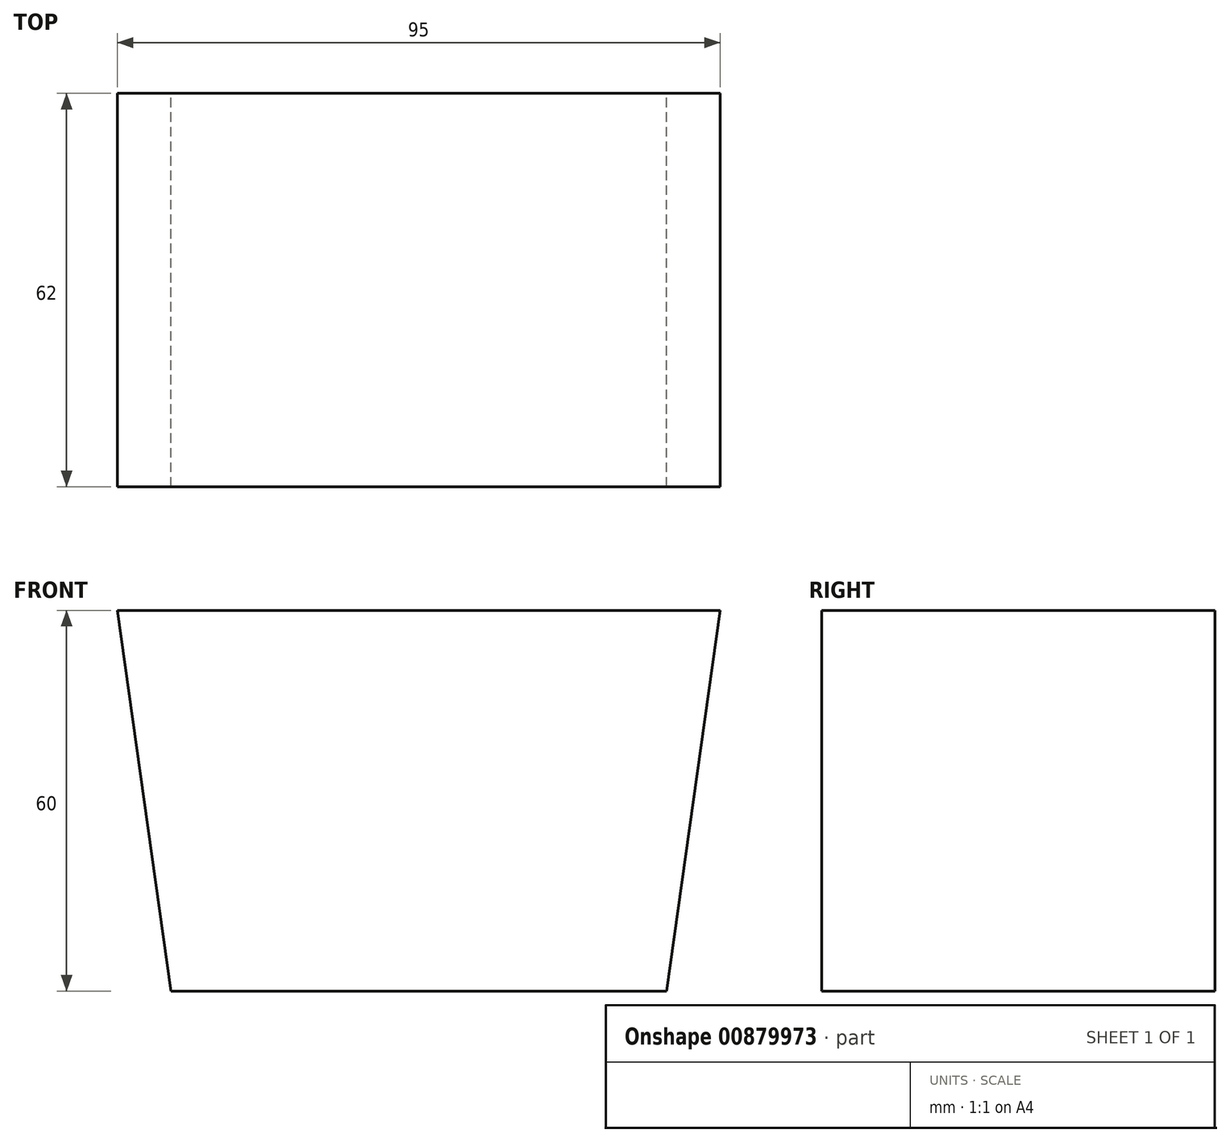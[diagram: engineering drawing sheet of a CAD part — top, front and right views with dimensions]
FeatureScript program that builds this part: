
annotation { "Feature Type Name" : "Feature", "Feature Type Description" : "" }
export const myFeature = defineFeature(function(context is Context, id is Id, definition is map)
    precondition{}
    {
        {
            var Q0;
            Q0=qCreatedBy(makeId("Front.planeOp"),FACE);
            var sketch = newSketch(context, id + "F0", { "sketchPlane" : qUnion([Q0])});
            skLineSegment(sketch, "E0.bottom", {"start": v(47.5, 30) * mm, "end": v(-47.5, 30) * mm});
            skLineSegment(sketch, "E0.top", {"start": v(39.07, -30) * mm, "end": v(-39.07, -30) * mm});
            skPoint(sketch, "E0.middle", {"position": v(0, 0) * mm});
            skLineSegment(sketch, "E1", {"start": v(-47.5, 30) * mm, "end": v(-39.07, -30) * mm});
            skLineSegment(sketch, "E2", {"start": v(47.5, 30) * mm, "end": v(39.07, -30) * mm});
            skPoint(sketch, "E3.orphan", {"position": v(-47.5, -30) * mm});
            skPoint(sketch, "E4.orphan", {"position": v(47.5, -30) * mm});
            skSolve(sketch);
        }
        {
            var Q0;
            Q0 = qSketchRegion(id + "F0", true);
            extrude(context, id + "F1", {"entities" : qUnion([Q0]), "depth" : 62 * mm, "offsetDistance" : 25 * mm});
        }
    });
